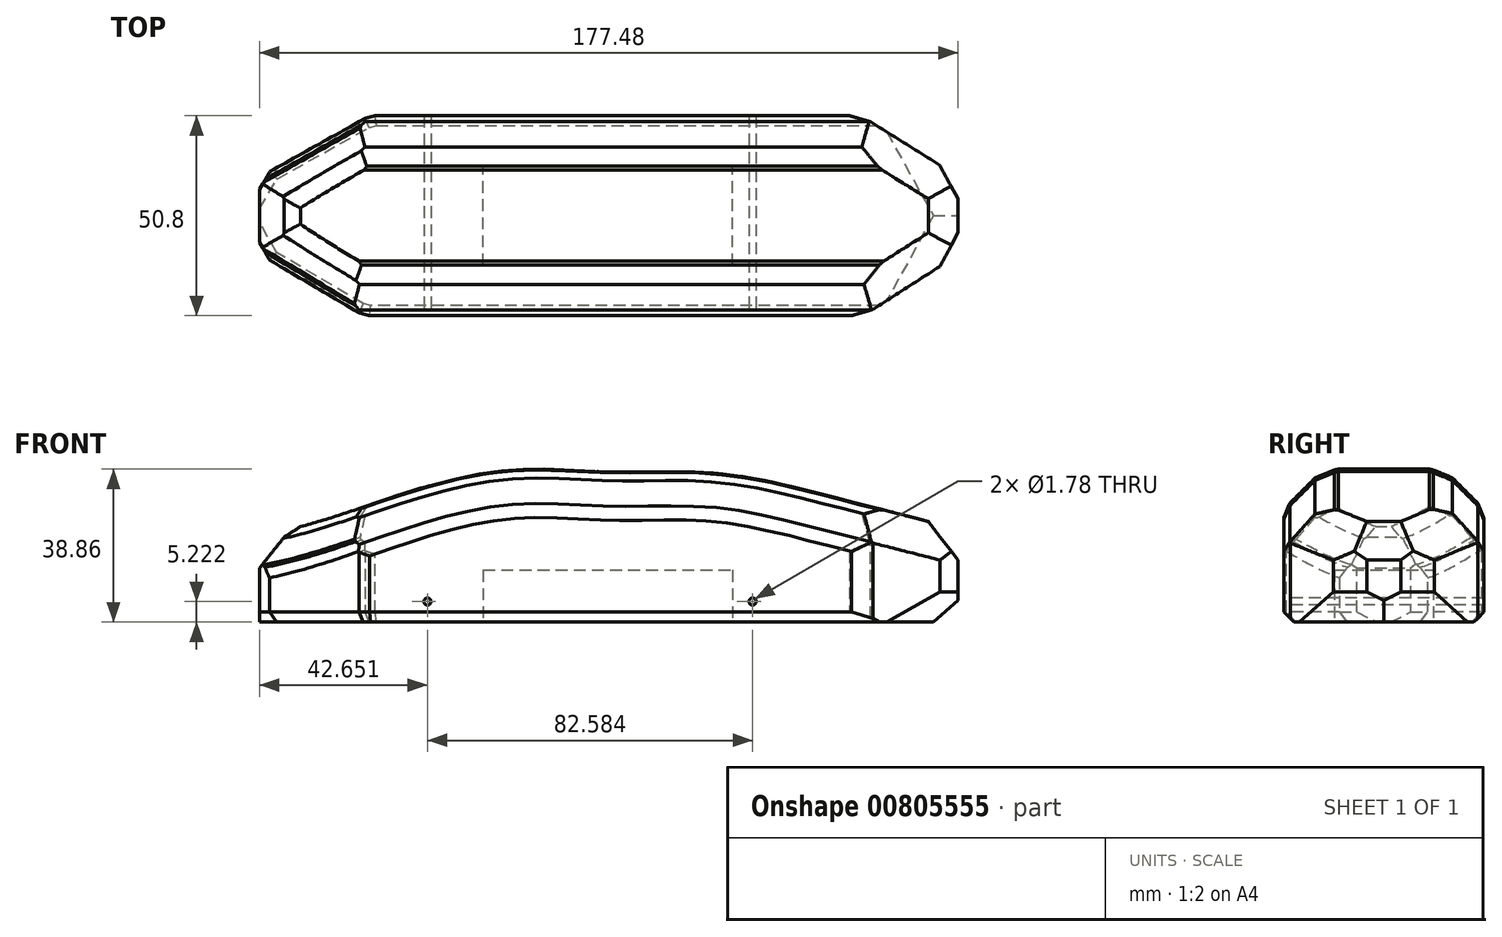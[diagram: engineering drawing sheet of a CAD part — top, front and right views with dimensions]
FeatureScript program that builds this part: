
annotation { "Feature Type Name" : "Feature", "Feature Type Description" : "" }
export const myFeature = defineFeature(function(context is Context, id is Id, definition is map)
    precondition{}
    {
        {
            var Q0;
            Q0=qCreatedBy(makeId("Top.planeOp"),FACE);
            var sketch = newSketch(context, id + "F0", { "sketchPlane" : qUnion([Q0])});
            skLineSegment(sketch, "E0.bottom", {"start": v(-88.9, -25.4) * mm, "end": v(88.9, -25.4) * mm});
            skLineSegment(sketch, "E0.top", {"start": v(-88.9, 25.4) * mm, "end": v(88.9, 25.4) * mm});
            skLineSegment(sketch, "E0.left", {"start": v(-88.9, -25.4) * mm, "end": v(-88.9, 25.4) * mm});
            skLineSegment(sketch, "E0.right", {"start": v(88.9, -25.4) * mm, "end": v(88.9, 25.4) * mm});
            skPoint(sketch, "E0.middle", {"position": v(0, 0) * mm});
            skSolve(sketch);
        }
        {
            var Q0;
            Q0=makeQuery(id+"F0.imprint","IMPRINT",FACE,{"disambiguationData":[TD([[makeQuery(id+"F0.imprint","IMPRINT",EDGE,{"derivedFrom":sQuery(id+"F0.wireOp",EDGE,"E0.bottom")}),1.0]])]});
            extrude(context, id + "F1", {"entities" : qUnion([Q0]), "depth" : 76.2 * mm, "offsetDistance" : 25.4 * mm});
        }
        {
            var Q0;
            Q0=qCreatedBy(makeId("Front.planeOp"),FACE);
            var sketch = newSketch(context, id + "F2", { "sketchPlane" : qUnion([Q0])});
            skFitSpline(sketch, "E1", {"points": [v(90.36, 23.16) * mm, v(58.43, 31.43) * mm, v(27.89, 37.74) * mm, v(0, 38.13) * mm, v(-23.16, 38.72) * mm, v(-52.87, 32.41) * mm, v(-89.76, 22.17) * mm], "startDerivative": vector(-174.93, 47.7) * mm, "endDerivative": vector(-202.04, -19.59) * mm});
            skArc(sketch, "E2", {"start": v(90.36, 23.16) * mm, "mid": v(-0.36, 142.7) * mm, "end": v(-89.76, 22.17) * mm});
            skSolve(sketch);
        }
        {
            var Q0;
            Q0 = qSketchRegion(id + "F2", true);
            extrude(context, id + "F3", {"entities" : qUnion([Q0]), "operationType" : NewBodyOperationType.REMOVE, "endBound" : BoundingType.SYMMETRIC, "depth" : 87.88 * mm, "offsetDistance" : 25.4 * mm});
        }
        {
            var Q0;
            Q0=qCreatedBy(makeId("Top.planeOp"),FACE);
            var sketch = newSketch(context, id + "F4", { "sketchPlane" : qUnion([Q0])});
            skLineSegment(sketch, "E3", {"start": v(-57.16, 27.3) * mm, "end": v(-88.58, 9.75) * mm});
            skLineSegment(sketch, "E4", {"start": v(-88.58, 9.75) * mm, "end": v(-88.58, 0) * mm});
            skLineSegment(sketch, "E5", {"start": v(-88.58, 0) * mm, "end": v(-88.58, -9.75) * mm});
            skLineSegment(sketch, "E6", {"start": v(-88.58, -9.75) * mm, "end": v(-57.16, -28.3) * mm});
            skArc(sketch, "E7", {"start": v(-57.16, 27.3) * mm, "mid": v(-128.15, -0.5) * mm, "end": v(-57.16, -28.3) * mm});
            skSolve(sketch);
        }
        {
            var Q0;
            Q0 = qSketchRegion(id + "F4", true);
            extrude(context, id + "F5", {"entities" : qUnion([Q0]), "operationType" : NewBodyOperationType.REMOVE, "endBound" : BoundingType.SYMMETRIC, "depth" : 72.64 * mm, "offsetDistance" : 25.4 * mm});
        }
        {
            var Q0;
            Q0=qCreatedBy(makeId("Top.planeOp"),FACE);
            var sketch = newSketch(context, id + "F6", { "sketchPlane" : qUnion([Q0])});
            skLineSegment(sketch, "E8", {"start": v(58.2, 29.15) * mm, "end": v(90.12, 9.16) * mm});
            skLineSegment(sketch, "E9", {"start": v(90.12, 9.16) * mm, "end": v(90.12, 0) * mm});
            skLineSegment(sketch, "E10", {"start": v(90.12, 0) * mm, "end": v(90.12, -9.08) * mm});
            skLineSegment(sketch, "E11", {"start": v(90.12, -9.08) * mm, "end": v(58.2, -29.66) * mm});
            skArc(sketch, "E12", {"start": v(58.2, -29.66) * mm, "mid": v(104.92, -0.26) * mm, "end": v(58.2, 29.15) * mm});
            skSolve(sketch);
        }
        {
            var Q0;
            Q0 = qSketchRegion(id + "F6", true);
            extrude(context, id + "F7", {"entities" : qUnion([Q0]), "operationType" : NewBodyOperationType.REMOVE, "endBound" : BoundingType.SYMMETRIC, "depth" : 93.98 * mm, "offsetDistance" : 25.4 * mm});
        }
        {
            var Q0;
            Q0=makeQuery(id+"F5.boolean.opBoolean","INTERSECT",EDGE,{"derivedFrom":[makeQuery(id+"F3.boolean.opBoolean","COPY",FACE,{"derivedFrom":makeQuery(id+"F3.opExtrude","SWEPT_FACE",FACE,{"disambiguationData":[OSD([sQuery(id+"F2.wireOp",EDGE,"E1")])]})}),makeQuery(id+"F5.opExtrude","SWEPT_FACE",FACE,{"disambiguationData":[OSD([sQuery(id+"F4.wireOp",EDGE,"E3")])]})]});
            var Q1;
            Q1=makeQuery(id+"F5.boolean.opBoolean","INTERSECT",EDGE,{"derivedFrom":[makeQuery(id+"F3.boolean.opBoolean","COPY",FACE,{"derivedFrom":makeQuery(id+"F3.opExtrude","SWEPT_FACE",FACE,{"disambiguationData":[OSD([sQuery(id+"F2.wireOp",EDGE,"E1")])]})}),makeQuery(id+"F5.opExtrude","SWEPT_FACE",FACE,{"disambiguationData":[OSD([sQuery(id+"F4.wireOp",EDGE,"E4"),sQuery(id+"F4.wireOp",EDGE,"E5")])]})]});
            var Q2;
            Q2=makeQuery(id+"F5.boolean.opBoolean","INTERSECT",EDGE,{"derivedFrom":[makeQuery(id+"F3.boolean.opBoolean","COPY",FACE,{"derivedFrom":makeQuery(id+"F3.opExtrude","SWEPT_FACE",FACE,{"disambiguationData":[OSD([sQuery(id+"F2.wireOp",EDGE,"E1")])]})}),makeQuery(id+"F5.opExtrude","SWEPT_FACE",FACE,{"disambiguationData":[OSD([sQuery(id+"F4.wireOp",EDGE,"E6")])]})]});
            chamfer(context, id + "F8", {"entities" : qUnion([Q0, Q1, Q2]), "width" : 10.16 * mm, "tangentPropagation" : true});
        }
        {
            var Q0;
            Q0=makeQuery(id+"F7.boolean.opBoolean","INTERSECT",EDGE,{"derivedFrom":[makeQuery(id+"F3.boolean.opBoolean","COPY",FACE,{"derivedFrom":makeQuery(id+"F3.opExtrude","SWEPT_FACE",FACE,{"disambiguationData":[OSD([sQuery(id+"F2.wireOp",EDGE,"E1")])]})}),makeQuery(id+"F7.opExtrude","SWEPT_FACE",FACE,{"disambiguationData":[OSD([sQuery(id+"F6.wireOp",EDGE,"E11")])]})]});
            var Q1;
            Q1=makeQuery(id+"F3.boolean.opBoolean","INTERSECT",EDGE,{"derivedFrom":[makeQuery(id+"F1.opExtrude","SWEPT_FACE",FACE,{"disambiguationData":[OSD([sQuery(id+"F0.wireOp",EDGE,"E0.right")])]}),makeQuery(id+"F3.opExtrude","SWEPT_FACE",FACE,{"disambiguationData":[OSD([sQuery(id+"F2.wireOp",EDGE,"E1")])]})]});
            var Q2;
            Q2=makeQuery(id+"F7.boolean.opBoolean","INTERSECT",EDGE,{"derivedFrom":[makeQuery(id+"F3.boolean.opBoolean","COPY",FACE,{"derivedFrom":makeQuery(id+"F3.opExtrude","SWEPT_FACE",FACE,{"disambiguationData":[OSD([sQuery(id+"F2.wireOp",EDGE,"E1")])]})}),makeQuery(id+"F7.opExtrude","SWEPT_FACE",FACE,{"disambiguationData":[OSD([sQuery(id+"F6.wireOp",EDGE,"E8")])]})]});
            var Q3;
            Q3=makeQuery(id+"F3.boolean.opBoolean","INTERSECT",EDGE,{"derivedFrom":[makeQuery(id+"F1.opExtrude","SWEPT_FACE",FACE,{"disambiguationData":[OSD([sQuery(id+"F0.wireOp",EDGE,"E0.bottom")])]}),makeQuery(id+"F3.opExtrude","SWEPT_FACE",FACE,{"disambiguationData":[OSD([sQuery(id+"F2.wireOp",EDGE,"E1")])]})]});
            var Q4;
            Q4=makeQuery(id+"F3.boolean.opBoolean","INTERSECT",EDGE,{"derivedFrom":[makeQuery(id+"F1.opExtrude","SWEPT_FACE",FACE,{"disambiguationData":[OSD([sQuery(id+"F0.wireOp",EDGE,"E0.top")])]}),makeQuery(id+"F3.opExtrude","SWEPT_FACE",FACE,{"disambiguationData":[OSD([sQuery(id+"F2.wireOp",EDGE,"E1")])]})]});
            chamfer(context, id + "F9", {"entities" : qUnion([Q0, Q1, Q2, Q3, Q4]), "width" : 10.16 * mm, "tangentPropagation" : true});
        }
        {
            var Q0;
            Q0=makeQuery(id+"F7.boolean.opBoolean","INTERSECT",EDGE,{"derivedFrom":[makeQuery(id+"F1.opExtrude","SWEPT_FACE",FACE,{"disambiguationData":[OSD([sQuery(id+"F0.wireOp",EDGE,"E0.bottom")])]}),makeQuery(id+"F7.opExtrude","SWEPT_FACE",FACE,{"disambiguationData":[OSD([sQuery(id+"F6.wireOp",EDGE,"E11")])]})]});
            var Q1;
            Q1=makeQuery(id+"F7.boolean.opBoolean","INTERSECT",EDGE,{"derivedFrom":[makeQuery(id+"F1.opExtrude","SWEPT_FACE",FACE,{"disambiguationData":[OSD([sQuery(id+"F0.wireOp",EDGE,"E0.right")])]}),makeQuery(id+"F7.opExtrude","SWEPT_FACE",FACE,{"disambiguationData":[OSD([sQuery(id+"F6.wireOp",EDGE,"E11")])]})]});
            var Q2;
            Q2=makeQuery(id+"F7.boolean.opBoolean","INTERSECT",EDGE,{"derivedFrom":[makeQuery(id+"F1.opExtrude","SWEPT_FACE",FACE,{"disambiguationData":[OSD([sQuery(id+"F0.wireOp",EDGE,"E0.right")])]}),makeQuery(id+"F7.opExtrude","SWEPT_FACE",FACE,{"disambiguationData":[OSD([sQuery(id+"F6.wireOp",EDGE,"E8")])]})]});
            var Q3;
            Q3=makeQuery(id+"F7.boolean.opBoolean","INTERSECT",EDGE,{"derivedFrom":[makeQuery(id+"F1.opExtrude","SWEPT_FACE",FACE,{"disambiguationData":[OSD([sQuery(id+"F0.wireOp",EDGE,"E0.top")])]}),makeQuery(id+"F7.opExtrude","SWEPT_FACE",FACE,{"disambiguationData":[OSD([sQuery(id+"F6.wireOp",EDGE,"E8")])]})]});
            chamfer(context, id + "F10", {"entities" : qUnion([Q0, Q1, Q2, Q3]), "width" : 10.16 * mm, "tangentPropagation" : true});
        }
        {
            var Q0;
            Q0=makeQuery(id+"F5.boolean.opBoolean","INTERSECT",EDGE,{"derivedFrom":[makeQuery(id+"F1.opExtrude","SWEPT_FACE",FACE,{"disambiguationData":[OSD([sQuery(id+"F0.wireOp",EDGE,"E0.top")])]}),makeQuery(id+"F5.opExtrude","SWEPT_FACE",FACE,{"disambiguationData":[OSD([sQuery(id+"F4.wireOp",EDGE,"E3")])]})]});
            var Q1;
            Q1=makeQuery(id+"F5.boolean.opBoolean","COPY",EDGE,{"derivedFrom":makeQuery(id+"F5.opExtrude","SWEPT_EDGE",EDGE,{"disambiguationData":[OSD([sQuery(id+"F4.wireOp",EDGE,"E3"),sQuery(id+"F4.wireOp",EDGE,"E4")])]})});
            var Q2;
            Q2=makeQuery(id+"F5.boolean.opBoolean","COPY",EDGE,{"derivedFrom":makeQuery(id+"F5.opExtrude","SWEPT_EDGE",EDGE,{"disambiguationData":[OSD([sQuery(id+"F4.wireOp",EDGE,"E5"),sQuery(id+"F4.wireOp",EDGE,"E6")])]})});
            var Q3;
            Q3=makeQuery(id+"F5.boolean.opBoolean","INTERSECT",EDGE,{"derivedFrom":[makeQuery(id+"F1.opExtrude","SWEPT_FACE",FACE,{"disambiguationData":[OSD([sQuery(id+"F0.wireOp",EDGE,"E0.bottom")])]}),makeQuery(id+"F5.opExtrude","SWEPT_FACE",FACE,{"disambiguationData":[OSD([sQuery(id+"F4.wireOp",EDGE,"E6")])]})]});
            var Q4;
            {var subQ0=makeQuery(id+"F5.opExtrude","SWEPT_FACE",FACE,{"disambiguationData":[OSD([sQuery(id+"F4.wireOp",EDGE,"E6")])]});Q4=makeQuery(id+"F8.opChamfer","BLEND_EDGE",EDGE,{"blendedFrom":[makeQuery(id+"F5.boolean.opBoolean","INTERSECT",EDGE,{"derivedFrom":[makeQuery(id+"F3.boolean.opBoolean","COPY",FACE,{"derivedFrom":makeQuery(id+"F3.opExtrude","SWEPT_FACE",FACE,{"disambiguationData":[OSD([sQuery(id+"F2.wireOp",EDGE,"E1")])]})}),subQ0]}),makeQuery(id+"F5.boolean.opBoolean","COPY",FACE,{"derivedFrom":subQ0})],"blendedInto":[makeQuery(id+"F5.boolean.opBoolean","COPY",FACE,{"derivedFrom":subQ0})]});}
            var Q5;
            {var subQ0=makeQuery(id+"F5.opExtrude","SWEPT_FACE",FACE,{"disambiguationData":[OSD([sQuery(id+"F4.wireOp",EDGE,"E3")])]});Q5=makeQuery(id+"F8.opChamfer","BLEND_EDGE",EDGE,{"blendedFrom":[makeQuery(id+"F5.boolean.opBoolean","INTERSECT",EDGE,{"derivedFrom":[makeQuery(id+"F3.boolean.opBoolean","COPY",FACE,{"derivedFrom":makeQuery(id+"F3.opExtrude","SWEPT_FACE",FACE,{"disambiguationData":[OSD([sQuery(id+"F2.wireOp",EDGE,"E1")])]})}),subQ0]}),makeQuery(id+"F5.boolean.opBoolean","COPY",FACE,{"derivedFrom":subQ0})],"blendedInto":[makeQuery(id+"F5.boolean.opBoolean","COPY",FACE,{"derivedFrom":subQ0})]});}
            chamfer(context, id + "F11", {"entities" : qUnion([Q0, Q1, Q2, Q3, Q4, Q5]), "width" : 5.08 * mm, "tangentPropagation" : true});
        }
        {
            var Q0;
            {var subQ0=makeQuery(id+"F1.opExtrude","SWEPT_FACE",FACE,{"disambiguationData":[OSD([sQuery(id+"F0.wireOp",EDGE,"E0.bottom")])]});Q0=makeQuery(id+"F9.opChamfer","BLEND_EDGE",EDGE,{"blendedFrom":[makeQuery(id+"F3.boolean.opBoolean","INTERSECT",EDGE,{"derivedFrom":[subQ0,makeQuery(id+"F3.opExtrude","SWEPT_FACE",FACE,{"disambiguationData":[OSD([sQuery(id+"F2.wireOp",EDGE,"E1")])]})]}),subQ0],"blendedInto":[subQ0]});}
            var Q1;
            {var subQ0=makeQuery(id+"F1.opExtrude","SWEPT_FACE",FACE,{"disambiguationData":[OSD([sQuery(id+"F0.wireOp",EDGE,"E0.top")])]});Q1=makeQuery(id+"F9.opChamfer","BLEND_EDGE",EDGE,{"blendedFrom":[makeQuery(id+"F3.boolean.opBoolean","INTERSECT",EDGE,{"derivedFrom":[subQ0,makeQuery(id+"F3.opExtrude","SWEPT_FACE",FACE,{"disambiguationData":[OSD([sQuery(id+"F2.wireOp",EDGE,"E1")])]})]}),subQ0],"blendedInto":[subQ0]});}
            chamfer(context, id + "F12", {"entities" : qUnion([Q0, Q1]), "width" : 5.08 * mm, "tangentPropagation" : true});
        }
        {
            var Q0;
            {var subQ0=makeQuery(id+"F3.boolean.opBoolean","COPY",FACE,{"derivedFrom":makeQuery(id+"F3.opExtrude","SWEPT_FACE",FACE,{"disambiguationData":[OSD([sQuery(id+"F2.wireOp",EDGE,"E1")])]})});Q0=makeQuery(id+"F8.opChamfer","BLEND_EDGE",EDGE,{"blendedFrom":[makeQuery(id+"F5.boolean.opBoolean","INTERSECT",EDGE,{"derivedFrom":[subQ0,makeQuery(id+"F5.opExtrude","SWEPT_FACE",FACE,{"disambiguationData":[OSD([sQuery(id+"F4.wireOp",EDGE,"E3")])]})]}),subQ0],"blendedInto":[subQ0]});}
            var Q1;
            {var subQ0=makeQuery(id+"F3.boolean.opBoolean","COPY",FACE,{"derivedFrom":makeQuery(id+"F3.opExtrude","SWEPT_FACE",FACE,{"disambiguationData":[OSD([sQuery(id+"F2.wireOp",EDGE,"E1")])]})});Q1=makeQuery(id+"F8.opChamfer","BLEND_EDGE",EDGE,{"blendedFrom":[makeQuery(id+"F5.boolean.opBoolean","INTERSECT",EDGE,{"derivedFrom":[subQ0,makeQuery(id+"F5.opExtrude","SWEPT_FACE",FACE,{"disambiguationData":[OSD([sQuery(id+"F4.wireOp",EDGE,"E6")])]})]}),subQ0],"blendedInto":[subQ0]});}
            var Q2;
            {var subQ0=makeQuery(id+"F3.boolean.opBoolean","COPY",FACE,{"derivedFrom":makeQuery(id+"F3.opExtrude","SWEPT_FACE",FACE,{"disambiguationData":[OSD([sQuery(id+"F2.wireOp",EDGE,"E1")])]})});Q2=makeQuery(id+"F8.opChamfer","BLEND_EDGE",EDGE,{"blendedFrom":[makeQuery(id+"F5.boolean.opBoolean","INTERSECT",EDGE,{"derivedFrom":[subQ0,makeQuery(id+"F5.opExtrude","SWEPT_FACE",FACE,{"disambiguationData":[OSD([sQuery(id+"F4.wireOp",EDGE,"E4"),sQuery(id+"F4.wireOp",EDGE,"E5")])]})]}),subQ0],"blendedInto":[subQ0]});}
            var Q3;
            {var subQ0=makeQuery(id+"F3.opExtrude","SWEPT_FACE",FACE,{"disambiguationData":[OSD([sQuery(id+"F2.wireOp",EDGE,"E1")])]});Q3=makeQuery(id+"F9.opChamfer","BLEND_EDGE",EDGE,{"blendedFrom":[makeQuery(id+"F3.boolean.opBoolean","INTERSECT",EDGE,{"derivedFrom":[makeQuery(id+"F1.opExtrude","SWEPT_FACE",FACE,{"disambiguationData":[OSD([sQuery(id+"F0.wireOp",EDGE,"E0.top")])]}),subQ0]}),makeQuery(id+"F3.boolean.opBoolean","COPY",FACE,{"derivedFrom":subQ0})],"blendedInto":[makeQuery(id+"F3.boolean.opBoolean","COPY",FACE,{"derivedFrom":subQ0})]});}
            var Q4;
            {var subQ0=makeQuery(id+"F3.opExtrude","SWEPT_FACE",FACE,{"disambiguationData":[OSD([sQuery(id+"F2.wireOp",EDGE,"E1")])]});Q4=makeQuery(id+"F9.opChamfer","BLEND_EDGE",EDGE,{"blendedFrom":[makeQuery(id+"F3.boolean.opBoolean","INTERSECT",EDGE,{"derivedFrom":[makeQuery(id+"F1.opExtrude","SWEPT_FACE",FACE,{"disambiguationData":[OSD([sQuery(id+"F0.wireOp",EDGE,"E0.bottom")])]}),subQ0]}),makeQuery(id+"F3.boolean.opBoolean","COPY",FACE,{"derivedFrom":subQ0})],"blendedInto":[makeQuery(id+"F3.boolean.opBoolean","COPY",FACE,{"derivedFrom":subQ0})]});}
            chamfer(context, id + "F13", {"entities" : qUnion([Q0, Q1, Q2, Q3, Q4]), "width" : 7.62 * mm, "tangentPropagation" : true});
        }
        {
            var Q0;
            {var subQ0=makeQuery(id+"F3.opExtrude","SWEPT_FACE",FACE,{"disambiguationData":[OSD([sQuery(id+"F2.wireOp",EDGE,"E1")])]});var subQ1=makeQuery(id+"F3.boolean.opBoolean","COPY",FACE,{"derivedFrom":subQ0});Q0=makeQuery(id+"F13.opChamfer","BLEND_EDGE",EDGE,{"blendedFrom":[makeQuery(id+"F9.opChamfer","BLEND_EDGE",EDGE,{"blendedFrom":[makeQuery(id+"F3.boolean.opBoolean","INTERSECT",EDGE,{"derivedFrom":[makeQuery(id+"F1.opExtrude","SWEPT_FACE",FACE,{"disambiguationData":[OSD([sQuery(id+"F0.wireOp",EDGE,"E0.top")])]}),subQ0]}),subQ1],"blendedInto":[subQ1]}),subQ1],"blendedInto":[subQ1]});}
            var Q1;
            {var subQ0=makeQuery(id+"F3.opExtrude","SWEPT_FACE",FACE,{"disambiguationData":[OSD([sQuery(id+"F2.wireOp",EDGE,"E1")])]});var subQ1=makeQuery(id+"F3.boolean.opBoolean","COPY",FACE,{"derivedFrom":subQ0});Q1=makeQuery(id+"F13.opChamfer","BLEND_EDGE",EDGE,{"blendedFrom":[makeQuery(id+"F9.opChamfer","BLEND_EDGE",EDGE,{"blendedFrom":[makeQuery(id+"F3.boolean.opBoolean","INTERSECT",EDGE,{"derivedFrom":[makeQuery(id+"F1.opExtrude","SWEPT_FACE",FACE,{"disambiguationData":[OSD([sQuery(id+"F0.wireOp",EDGE,"E0.bottom")])]}),subQ0]}),subQ1],"blendedInto":[subQ1]}),subQ1],"blendedInto":[subQ1]});}
            chamfer(context, id + "F14", {"entities" : qUnion([Q0, Q1]), "width" : 2.54 * mm, "tangentPropagation" : true});
        }
        {
            var Q0;
            Q0=makeQuery(id+"F11.opChamfer","BLEND_EDGE",EDGE,{"blendedFrom":[makeQuery(id+"F5.boolean.opBoolean","COPY",EDGE,{"derivedFrom":makeQuery(id+"F5.opExtrude","SWEPT_EDGE",EDGE,{"disambiguationData":[OSD([sQuery(id+"F4.wireOp",EDGE,"E5"),sQuery(id+"F4.wireOp",EDGE,"E6")])]})}),makeQuery(id+"F1.opExtrude","CAP_FACE",FACE,{"disambiguationData":[OSD([sQuery(id+"F0.wireOp",EDGE,"E0.bottom"),sQuery(id+"F0.wireOp",EDGE,"E0.top"),sQuery(id+"F0.wireOp",EDGE,"E0.left"),sQuery(id+"F0.wireOp",EDGE,"E0.right")])],"isStart":true})],"blendedInto":[makeQuery(id+"F1.opExtrude","CAP_FACE",FACE,{"disambiguationData":[OSD([sQuery(id+"F0.wireOp",EDGE,"E0.bottom"),sQuery(id+"F0.wireOp",EDGE,"E0.top"),sQuery(id+"F0.wireOp",EDGE,"E0.left"),sQuery(id+"F0.wireOp",EDGE,"E0.right")])],"isStart":true})]});
            var Q1;
            Q1=makeQuery(id+"F11.opChamfer","BLEND_EDGE",EDGE,{"blendedFrom":[makeQuery(id+"F5.boolean.opBoolean","COPY",EDGE,{"derivedFrom":makeQuery(id+"F5.opExtrude","SWEPT_EDGE",EDGE,{"disambiguationData":[OSD([sQuery(id+"F4.wireOp",EDGE,"E3"),sQuery(id+"F4.wireOp",EDGE,"E4")])]})}),makeQuery(id+"F1.opExtrude","CAP_FACE",FACE,{"disambiguationData":[OSD([sQuery(id+"F0.wireOp",EDGE,"E0.bottom"),sQuery(id+"F0.wireOp",EDGE,"E0.top"),sQuery(id+"F0.wireOp",EDGE,"E0.left"),sQuery(id+"F0.wireOp",EDGE,"E0.right")])],"isStart":true})],"blendedInto":[makeQuery(id+"F1.opExtrude","CAP_FACE",FACE,{"disambiguationData":[OSD([sQuery(id+"F0.wireOp",EDGE,"E0.bottom"),sQuery(id+"F0.wireOp",EDGE,"E0.top"),sQuery(id+"F0.wireOp",EDGE,"E0.left"),sQuery(id+"F0.wireOp",EDGE,"E0.right")])],"isStart":true})]});
            var Q2;
            Q2=makeQuery(id+"F5.boolean.opBoolean","INTERSECT",EDGE,{"derivedFrom":[makeQuery(id+"F1.opExtrude","CAP_FACE",FACE,{"disambiguationData":[OSD([sQuery(id+"F0.wireOp",EDGE,"E0.bottom"),sQuery(id+"F0.wireOp",EDGE,"E0.top"),sQuery(id+"F0.wireOp",EDGE,"E0.left"),sQuery(id+"F0.wireOp",EDGE,"E0.right")])],"isStart":true}),makeQuery(id+"F5.opExtrude","SWEPT_FACE",FACE,{"disambiguationData":[OSD([sQuery(id+"F4.wireOp",EDGE,"E3")])]})]});
            var Q3;
            {var subQ0=sQuery(id+"F0.wireOp",EDGE,"E0.top");Q3=makeQuery(id+"F11.opChamfer","BLEND_EDGE",EDGE,{"blendedFrom":[makeQuery(id+"F5.boolean.opBoolean","INTERSECT",EDGE,{"derivedFrom":[makeQuery(id+"F1.opExtrude","SWEPT_FACE",FACE,{"disambiguationData":[OSD([subQ0])]}),makeQuery(id+"F5.opExtrude","SWEPT_FACE",FACE,{"disambiguationData":[OSD([sQuery(id+"F4.wireOp",EDGE,"E3")])]})]}),makeQuery(id+"F1.opExtrude","CAP_FACE",FACE,{"disambiguationData":[OSD([sQuery(id+"F0.wireOp",EDGE,"E0.bottom"),subQ0,sQuery(id+"F0.wireOp",EDGE,"E0.left"),sQuery(id+"F0.wireOp",EDGE,"E0.right")])],"isStart":true})],"blendedInto":[makeQuery(id+"F1.opExtrude","CAP_FACE",FACE,{"disambiguationData":[OSD([sQuery(id+"F0.wireOp",EDGE,"E0.bottom"),subQ0,sQuery(id+"F0.wireOp",EDGE,"E0.left"),sQuery(id+"F0.wireOp",EDGE,"E0.right")])],"isStart":true})]});}
            var Q4;
            Q4=makeQuery(id+"F5.boolean.opBoolean","INTERSECT",EDGE,{"derivedFrom":[makeQuery(id+"F1.opExtrude","CAP_FACE",FACE,{"disambiguationData":[OSD([sQuery(id+"F0.wireOp",EDGE,"E0.bottom"),sQuery(id+"F0.wireOp",EDGE,"E0.top"),sQuery(id+"F0.wireOp",EDGE,"E0.left"),sQuery(id+"F0.wireOp",EDGE,"E0.right")])],"isStart":true}),makeQuery(id+"F5.opExtrude","SWEPT_FACE",FACE,{"disambiguationData":[OSD([sQuery(id+"F4.wireOp",EDGE,"E6")])]})]});
            var Q5;
            {var subQ0=sQuery(id+"F0.wireOp",EDGE,"E0.bottom");Q5=makeQuery(id+"F11.opChamfer","BLEND_EDGE",EDGE,{"blendedFrom":[makeQuery(id+"F5.boolean.opBoolean","INTERSECT",EDGE,{"derivedFrom":[makeQuery(id+"F1.opExtrude","SWEPT_FACE",FACE,{"disambiguationData":[OSD([subQ0])]}),makeQuery(id+"F5.opExtrude","SWEPT_FACE",FACE,{"disambiguationData":[OSD([sQuery(id+"F4.wireOp",EDGE,"E6")])]})]}),makeQuery(id+"F1.opExtrude","CAP_FACE",FACE,{"disambiguationData":[OSD([subQ0,sQuery(id+"F0.wireOp",EDGE,"E0.top"),sQuery(id+"F0.wireOp",EDGE,"E0.left"),sQuery(id+"F0.wireOp",EDGE,"E0.right")])],"isStart":true})],"blendedInto":[makeQuery(id+"F1.opExtrude","CAP_FACE",FACE,{"disambiguationData":[OSD([subQ0,sQuery(id+"F0.wireOp",EDGE,"E0.top"),sQuery(id+"F0.wireOp",EDGE,"E0.left"),sQuery(id+"F0.wireOp",EDGE,"E0.right")])],"isStart":true})]});}
            var Q6;
            Q6=makeQuery(id+"F1.opExtrude","CAP_EDGE",EDGE,{"disambiguationData":[OSD([sQuery(id+"F0.wireOp",EDGE,"E0.bottom")])],"isStart":true});
            var Q7;
            Q7=makeQuery(id+"F1.opExtrude","CAP_EDGE",EDGE,{"disambiguationData":[OSD([sQuery(id+"F0.wireOp",EDGE,"E0.top")])],"isStart":true});
            chamfer(context, id + "F15", {"entities" : qUnion([Q0, Q1, Q2, Q3, Q4, Q5, Q6, Q7]), "width" : 2.54 * mm, "tangentPropagation" : true});
        }
        {
            var Q0;
            {var subQ0=sQuery(id+"F0.wireOp",EDGE,"E0.bottom");Q0=makeQuery(id+"F10.opChamfer","BLEND_EDGE",EDGE,{"blendedFrom":[makeQuery(id+"F7.boolean.opBoolean","INTERSECT",EDGE,{"derivedFrom":[makeQuery(id+"F1.opExtrude","SWEPT_FACE",FACE,{"disambiguationData":[OSD([subQ0])]}),makeQuery(id+"F7.opExtrude","SWEPT_FACE",FACE,{"disambiguationData":[OSD([sQuery(id+"F6.wireOp",EDGE,"E11")])]})]}),makeQuery(id+"F1.opExtrude","CAP_FACE",FACE,{"disambiguationData":[OSD([subQ0,sQuery(id+"F0.wireOp",EDGE,"E0.top"),sQuery(id+"F0.wireOp",EDGE,"E0.left"),sQuery(id+"F0.wireOp",EDGE,"E0.right")])],"isStart":true})],"blendedInto":[makeQuery(id+"F1.opExtrude","CAP_FACE",FACE,{"disambiguationData":[OSD([subQ0,sQuery(id+"F0.wireOp",EDGE,"E0.top"),sQuery(id+"F0.wireOp",EDGE,"E0.left"),sQuery(id+"F0.wireOp",EDGE,"E0.right")])],"isStart":true})]});}
            var Q1;
            {var subQ0=sQuery(id+"F0.wireOp",EDGE,"E0.top");Q1=makeQuery(id+"F10.opChamfer","BLEND_EDGE",EDGE,{"blendedFrom":[makeQuery(id+"F7.boolean.opBoolean","INTERSECT",EDGE,{"derivedFrom":[makeQuery(id+"F1.opExtrude","SWEPT_FACE",FACE,{"disambiguationData":[OSD([subQ0])]}),makeQuery(id+"F7.opExtrude","SWEPT_FACE",FACE,{"disambiguationData":[OSD([sQuery(id+"F6.wireOp",EDGE,"E8")])]})]}),makeQuery(id+"F1.opExtrude","CAP_FACE",FACE,{"disambiguationData":[OSD([sQuery(id+"F0.wireOp",EDGE,"E0.bottom"),subQ0,sQuery(id+"F0.wireOp",EDGE,"E0.left"),sQuery(id+"F0.wireOp",EDGE,"E0.right")])],"isStart":true})],"blendedInto":[makeQuery(id+"F1.opExtrude","CAP_FACE",FACE,{"disambiguationData":[OSD([sQuery(id+"F0.wireOp",EDGE,"E0.bottom"),subQ0,sQuery(id+"F0.wireOp",EDGE,"E0.left"),sQuery(id+"F0.wireOp",EDGE,"E0.right")])],"isStart":true})]});}
            var Q2;
            {var subQ0=sQuery(id+"F0.wireOp",EDGE,"E0.right");Q2=makeQuery(id+"F10.opChamfer","BLEND_EDGE",EDGE,{"blendedFrom":[makeQuery(id+"F7.boolean.opBoolean","INTERSECT",EDGE,{"derivedFrom":[makeQuery(id+"F1.opExtrude","SWEPT_FACE",FACE,{"disambiguationData":[OSD([subQ0])]}),makeQuery(id+"F7.opExtrude","SWEPT_FACE",FACE,{"disambiguationData":[OSD([sQuery(id+"F6.wireOp",EDGE,"E8")])]})]}),makeQuery(id+"F1.opExtrude","CAP_FACE",FACE,{"disambiguationData":[OSD([sQuery(id+"F0.wireOp",EDGE,"E0.bottom"),sQuery(id+"F0.wireOp",EDGE,"E0.top"),sQuery(id+"F0.wireOp",EDGE,"E0.left"),subQ0])],"isStart":true})],"blendedInto":[makeQuery(id+"F1.opExtrude","CAP_FACE",FACE,{"disambiguationData":[OSD([sQuery(id+"F0.wireOp",EDGE,"E0.bottom"),sQuery(id+"F0.wireOp",EDGE,"E0.top"),sQuery(id+"F0.wireOp",EDGE,"E0.left"),subQ0])],"isStart":true})]});}
            var Q3;
            {var subQ0=sQuery(id+"F0.wireOp",EDGE,"E0.right");Q3=makeQuery(id+"F10.opChamfer","BLEND_EDGE",EDGE,{"blendedFrom":[makeQuery(id+"F7.boolean.opBoolean","INTERSECT",EDGE,{"derivedFrom":[makeQuery(id+"F1.opExtrude","SWEPT_FACE",FACE,{"disambiguationData":[OSD([subQ0])]}),makeQuery(id+"F7.opExtrude","SWEPT_FACE",FACE,{"disambiguationData":[OSD([sQuery(id+"F6.wireOp",EDGE,"E11")])]})]}),makeQuery(id+"F1.opExtrude","CAP_FACE",FACE,{"disambiguationData":[OSD([sQuery(id+"F0.wireOp",EDGE,"E0.bottom"),sQuery(id+"F0.wireOp",EDGE,"E0.top"),sQuery(id+"F0.wireOp",EDGE,"E0.left"),subQ0])],"isStart":true})],"blendedInto":[makeQuery(id+"F1.opExtrude","CAP_FACE",FACE,{"disambiguationData":[OSD([sQuery(id+"F0.wireOp",EDGE,"E0.bottom"),sQuery(id+"F0.wireOp",EDGE,"E0.top"),sQuery(id+"F0.wireOp",EDGE,"E0.left"),subQ0])],"isStart":true})]});}
            chamfer(context, id + "F16", {"entities" : qUnion([Q0, Q1, Q2, Q3]), "width" : 7.62 * mm, "tangentPropagation" : true});
        }
        {
            var Q0;
            {var subQ0=sQuery(id+"F4.wireOp",EDGE,"E6");var subQ1=sQuery(id+"F2.wireOp",EDGE,"E1");var subQ2=makeQuery(id+"F5.opExtrude","SWEPT_FACE",FACE,{"disambiguationData":[OSD([subQ0])]});Q0=makeQuery(id+"F11.opChamfer","BLEND_EDGE",EDGE,{"blendedFrom":[makeQuery(id+"F8.opChamfer","BLEND_EDGE",EDGE,{"blendedFrom":[makeQuery(id+"F5.boolean.opBoolean","INTERSECT",EDGE,{"derivedFrom":[makeQuery(id+"F3.boolean.opBoolean","COPY",FACE,{"derivedFrom":makeQuery(id+"F3.opExtrude","SWEPT_FACE",FACE,{"disambiguationData":[OSD([subQ1])]})}),subQ2]}),makeQuery(id+"F5.boolean.opBoolean","COPY",FACE,{"derivedFrom":subQ2})],"blendedInto":[makeQuery(id+"F5.boolean.opBoolean","COPY",FACE,{"derivedFrom":subQ2})]}),makeQuery(id+"F8.opChamfer","BLEND_FACE",FACE,{"disambiguationData":[OSD([subQ1,subQ0])]})],"blendedInto":[makeQuery(id+"F8.opChamfer","BLEND_FACE",FACE,{"disambiguationData":[OSD([subQ1,subQ0])]})]});}
            var Q1;
            {var subQ0=sQuery(id+"F4.wireOp",EDGE,"E3");var subQ1=sQuery(id+"F2.wireOp",EDGE,"E1");var subQ2=makeQuery(id+"F5.opExtrude","SWEPT_FACE",FACE,{"disambiguationData":[OSD([subQ0])]});Q1=makeQuery(id+"F11.opChamfer","BLEND_EDGE",EDGE,{"blendedFrom":[makeQuery(id+"F8.opChamfer","BLEND_EDGE",EDGE,{"blendedFrom":[makeQuery(id+"F5.boolean.opBoolean","INTERSECT",EDGE,{"derivedFrom":[makeQuery(id+"F3.boolean.opBoolean","COPY",FACE,{"derivedFrom":makeQuery(id+"F3.opExtrude","SWEPT_FACE",FACE,{"disambiguationData":[OSD([subQ1])]})}),subQ2]}),makeQuery(id+"F5.boolean.opBoolean","COPY",FACE,{"derivedFrom":subQ2})],"blendedInto":[makeQuery(id+"F5.boolean.opBoolean","COPY",FACE,{"derivedFrom":subQ2})]}),makeQuery(id+"F8.opChamfer","BLEND_FACE",FACE,{"disambiguationData":[OSD([subQ1,subQ0])]})],"blendedInto":[makeQuery(id+"F8.opChamfer","BLEND_FACE",FACE,{"disambiguationData":[OSD([subQ1,subQ0])]})]});}
            chamfer(context, id + "F17", {"entities" : qUnion([Q0, Q1]), "width" : 2.54 * mm, "tangentPropagation" : true});
        }
        {
            var Q0;
            Q0=qCreatedBy(makeId("Top.planeOp"),FACE);
            var sketch = newSketch(context, id + "F18", { "sketchPlane" : qUnion([Q0])});
            skLineSegment(sketch, "E13", {"start": v(-31.75, 12.61) * mm, "end": v(31.59, 12.61) * mm});
            skLineSegment(sketch, "E14", {"start": v(31.59, 12.61) * mm, "end": v(31.59, -2.58) * mm});
            skLineSegment(sketch, "E15", {"start": v(-31.75, -12.61) * mm, "end": v(-31.75, 12.61) * mm});
            skLineSegment(sketch, "E16", {"start": v(-67.73, 0) * mm, "end": v(64.51, 0) * mm, "construction": true});
            skLineSegment(sketch, "E17.MirrorCS", {"start": v(0, 4.95) * mm, "end": v(0, -12.61) * mm});
            skLineSegment(sketch, "E18.MirrorCS", {"start": v(-31.75, -12.61) * mm, "end": v(31.59, -12.61) * mm});
            skLineSegment(sketch, "E19.MirrorCS", {"start": v(31.59, -12.61) * mm, "end": v(31.59, 2.58) * mm});
            skSolve(sketch);
        }
        {
            var Q0;
            Q0 = qSketchRegion(id + "F18", true);
            extrude(context, id + "F19", {"entities" : qUnion([Q0]), "operationType" : NewBodyOperationType.REMOVE, "depth" : 13.2 * mm, "offsetDistance" : 25.4 * mm});
        }
        {
            var Q0;
            Q0=makeQuery(id+"F1.opExtrude","SWEPT_FACE",FACE,{"disambiguationData":[OSD([sQuery(id+"F0.wireOp",EDGE,"E0.bottom")])]});
            var sketch = newSketch(context, id + "F20", { "sketchPlane" : qUnion([Q0])});
            skCircle(sketch, "E20", {"center": v(-45.93, 5.22) * mm, "radius": 0.89 * mm});
            skSolve(sketch);
        }
        {
            var Q0;
            Q0=makeQuery(id+"F20.imprint","IMPRINT",FACE,{"disambiguationData":[TD([[makeQuery(id+"F20.imprint","IMPRINT",EDGE,{"derivedFrom":sQuery(id+"F20.wireOp",EDGE,"E20")}),1.0]])]});
            extrude(context, id + "F21", {"entities" : qUnion([Q0]), "operationType" : NewBodyOperationType.REMOVE, "oppositeDirection" : true, "depth" : 127 * mm, "offsetDistance" : 25.4 * mm});
        }
        {
            var Q0;
            Q0=makeQuery(id+"F1.opExtrude","SWEPT_FACE",FACE,{"disambiguationData":[OSD([sQuery(id+"F0.wireOp",EDGE,"E0.bottom")])]});
            var sketch = newSketch(context, id + "F22", { "sketchPlane" : qUnion([Q0])});
            skCircle(sketch, "E21", {"center": v(36.65, 5.22) * mm, "radius": 0.89 * mm});
            skLineSegment(sketch, "E22", {"start": v(36.65, 5.22) * mm, "end": v(-45.93, 5.22) * mm, "construction": true});
            skSolve(sketch);
        }
        {
            var Q0;
            Q0=makeQuery(id+"F22.imprint","IMPRINT",FACE,{"disambiguationData":[TD([[makeQuery(id+"F22.imprint","IMPRINT",EDGE,{"derivedFrom":sQuery(id+"F22.wireOp",EDGE,"E21")}),1.0]])]});
            extrude(context, id + "F23", {"entities" : qUnion([Q0]), "operationType" : NewBodyOperationType.REMOVE, "oppositeDirection" : true, "depth" : 76.2 * mm, "offsetDistance" : 25.4 * mm});
        }
    });
